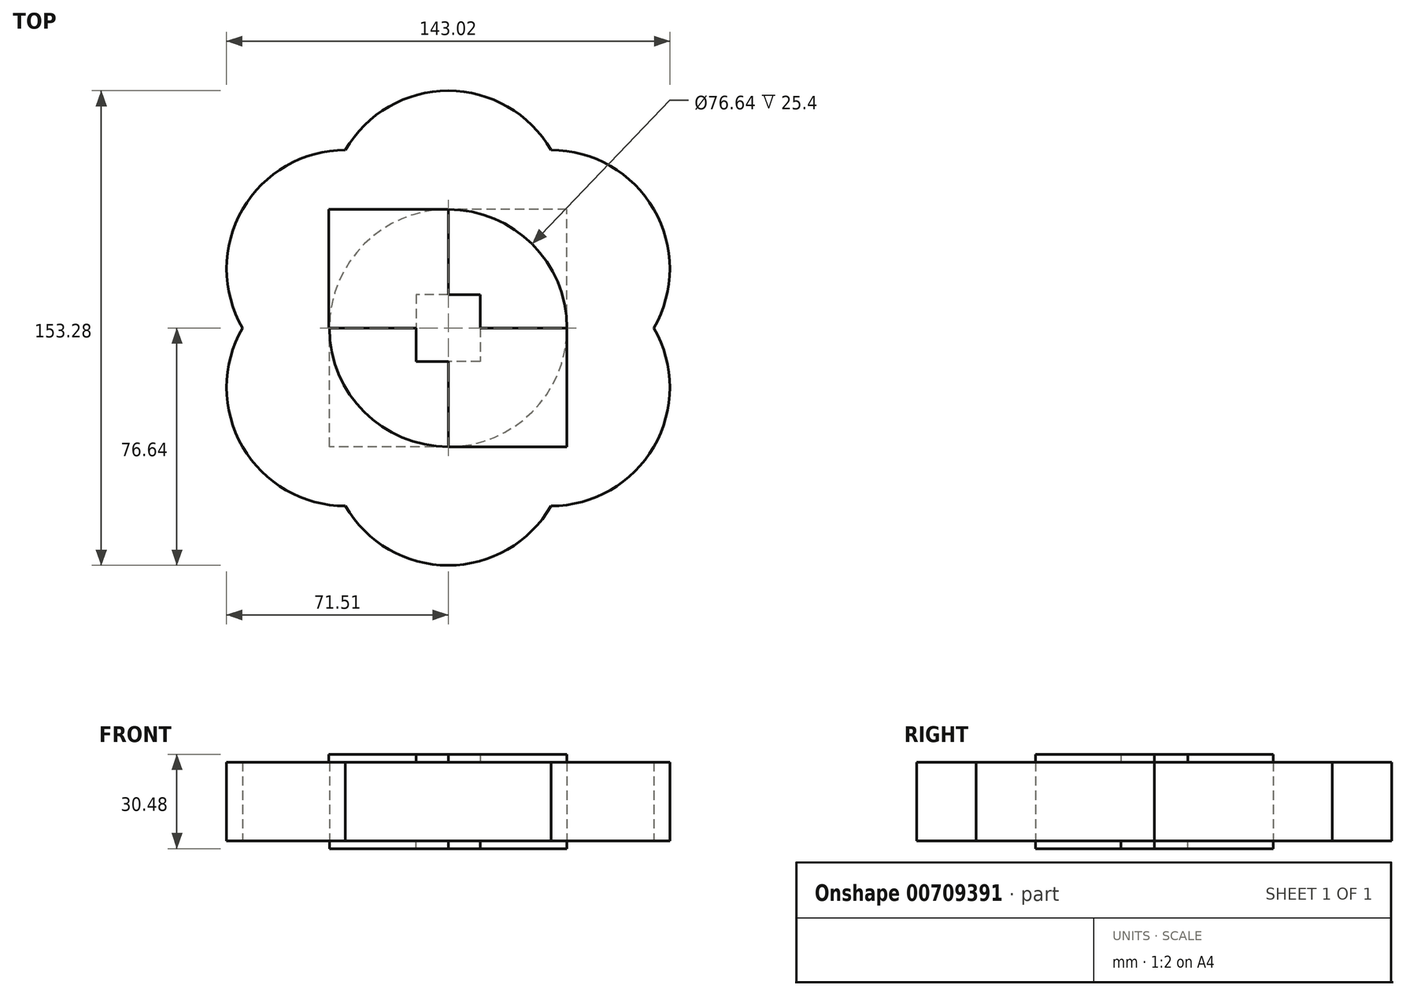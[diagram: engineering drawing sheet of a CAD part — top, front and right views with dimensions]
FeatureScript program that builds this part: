
annotation { "Feature Type Name" : "Feature", "Feature Type Description" : "" }
export const myFeature = defineFeature(function(context is Context, id is Id, definition is map)
    precondition{}
    {
        {
            var Q0;
            Q0=qCreatedBy(makeId("Top.planeOp"),FACE);
            var sketch = newSketch(context, id + "F0", { "sketchPlane" : qUnion([Q0])});
            skCircle(sketch, "E0", {"center": v(0, 0) * mm, "radius": 38.32 * mm});
            skCircle(sketch, "E1", {"center": v(0, 38.32) * mm, "radius": 38.32 * mm});
            skCircle(sketch, "E2", {"center": v(33.19, 19.16) * mm, "radius": 38.32 * mm});
            skCircle(sketch, "E3", {"center": v(33.19, -19.16) * mm, "radius": 38.32 * mm});
            skCircle(sketch, "E4", {"center": v(0, -38.32) * mm, "radius": 38.32 * mm});
            skCircle(sketch, "E5", {"center": v(-33.19, -19.16) * mm, "radius": 38.32 * mm});
            skCircle(sketch, "E6", {"center": v(-33.19, 19.16) * mm, "radius": 38.32 * mm});
            skSolve(sketch);
        }
        {
            var Q0;
            Q0 = qSketchRegion(id + "F0", true);
            extrude(context, id + "F1", {"entities" : qUnion([Q0]), "depth" : 25.4 * mm, "offsetDistance" : 25.4 * mm});
        }
        {
            var Q0;
            Q0=makeQuery(id+"F1.opExtrude","CAP_FACE",FACE,{"disambiguationData":[OSD([sQuery(id+"F0.wireOp",EDGE,"E0"),sQuery(id+"F0.wireOp",EDGE,"E1"),sQuery(id+"F0.wireOp",EDGE,"E2"),sQuery(id+"F0.wireOp",EDGE,"E3"),sQuery(id+"F0.wireOp",EDGE,"E4"),sQuery(id+"F0.wireOp",EDGE,"E5"),sQuery(id+"F0.wireOp",EDGE,"E6")])],"isStart":false});
            var sketch = newSketch(context, id + "F2", { "sketchPlane" : qUnion([Q0])});
            skPoint(sketch, "E7.center.orphan", {"position": v(38.32, 0) * mm});
            skPoint(sketch, "E8.center.orphan", {"position": v(0, -38.32) * mm});
            skPoint(sketch, "E9.center.orphan", {"position": v(0, 38.32) * mm});
            skPoint(sketch, "E10.center.orphan", {"position": v(-38.32, 0) * mm});
            skLineSegment(sketch, "E11.bottom", {"start": v(0, 0) * mm, "end": v(-38.51, 0) * mm});
            skLineSegment(sketch, "E11.top", {"start": v(0, 38.32) * mm, "end": v(-38.51, 38.32) * mm});
            skLineSegment(sketch, "E11.left", {"start": v(0, 0) * mm, "end": v(0, 38.32) * mm});
            skLineSegment(sketch, "E11.right", {"start": v(-38.51, 0) * mm, "end": v(-38.51, 38.32) * mm});
            skLineSegment(sketch, "E12.bottom", {"start": v(38.32, 0) * mm, "end": v(0, 0) * mm});
            skLineSegment(sketch, "E12.top", {"start": v(38.32, -38.32) * mm, "end": v(0, -38.32) * mm});
            skLineSegment(sketch, "E12.left", {"start": v(38.32, 0) * mm, "end": v(38.32, -38.32) * mm});
            skLineSegment(sketch, "E12.right", {"start": v(0, 0) * mm, "end": v(0, -38.32) * mm});
            skLineSegment(sketch, "E13.bottom", {"start": v(10.34, 10.79) * mm, "end": v(-10.34, 10.79) * mm});
            skLineSegment(sketch, "E13.top", {"start": v(10.34, -10.79) * mm, "end": v(-10.34, -10.79) * mm});
            skLineSegment(sketch, "E13.left", {"start": v(10.34, 10.79) * mm, "end": v(10.34, -10.79) * mm});
            skLineSegment(sketch, "E13.right", {"start": v(-10.34, 10.79) * mm, "end": v(-10.34, -10.79) * mm});
            skPoint(sketch, "E13.middle", {"position": v(0, 0) * mm});
            skSolve(sketch);
        }
        {
            var Q0;
            Q0 = qSketchRegion(id + "F2", true);
            extrude(context, id + "F3", {"entities" : qUnion([Q0]), "operationType" : NewBodyOperationType.ADD, "depth" : 2.54 * mm, "offsetDistance" : 25.4 * mm});
        }
        {
            var Q0;
            Q0=makeQuery(id+"F1.opExtrude","CAP_FACE",FACE,{"disambiguationData":[OSD([sQuery(id+"F0.wireOp",EDGE,"E0"),sQuery(id+"F0.wireOp",EDGE,"E1"),sQuery(id+"F0.wireOp",EDGE,"E2"),sQuery(id+"F0.wireOp",EDGE,"E3"),sQuery(id+"F0.wireOp",EDGE,"E4"),sQuery(id+"F0.wireOp",EDGE,"E5"),sQuery(id+"F0.wireOp",EDGE,"E6")])],"isStart":true});
            var sketch = newSketch(context, id + "F4", { "sketchPlane" : qUnion([Q0])});
            skPoint(sketch, "E14.bottom.start.orphan", {"position": v(-38.32, 0) * mm});
            skPoint(sketch, "E14.right.end.orphan", {"position": v(0, -38.32) * mm});
            skPoint(sketch, "E15.right.end.orphan", {"position": v(38.32, 0) * mm});
            skPoint(sketch, "E15.bottom.start.orphan", {"position": v(0, 38.32) * mm});
            skLineSegment(sketch, "E16.bottom", {"start": v(0, 38.32) * mm, "end": v(-38.32, 38.32) * mm});
            skLineSegment(sketch, "E16.top", {"start": v(0, 0) * mm, "end": v(-38.32, 0) * mm});
            skLineSegment(sketch, "E16.left", {"start": v(0, 38.32) * mm, "end": v(0, 0) * mm});
            skLineSegment(sketch, "E16.right", {"start": v(-38.32, 38.32) * mm, "end": v(-38.32, 0) * mm});
            skLineSegment(sketch, "E17.bottom", {"start": v(38.32, 0) * mm, "end": v(0, 0) * mm});
            skLineSegment(sketch, "E17.top", {"start": v(38.32, -38.32) * mm, "end": v(0, -38.32) * mm});
            skLineSegment(sketch, "E17.left", {"start": v(38.32, 0) * mm, "end": v(38.32, -38.32) * mm});
            skLineSegment(sketch, "E17.right", {"start": v(0, 0) * mm, "end": v(0, -38.32) * mm});
            skLineSegment(sketch, "E18.bottom", {"start": v(10.35, -10.79) * mm, "end": v(-10.35, -10.79) * mm});
            skLineSegment(sketch, "E18.top", {"start": v(10.35, 10.79) * mm, "end": v(-10.35, 10.79) * mm});
            skLineSegment(sketch, "E18.left", {"start": v(10.35, -10.79) * mm, "end": v(10.35, 10.79) * mm});
            skLineSegment(sketch, "E18.right", {"start": v(-10.35, -10.79) * mm, "end": v(-10.35, 10.79) * mm});
            skPoint(sketch, "E18.middle", {"position": v(0, 0) * mm});
            skSolve(sketch);
        }
        {
            var Q0;
            Q0 = qSketchRegion(id + "F4", true);
            extrude(context, id + "F5", {"entities" : qUnion([Q0]), "operationType" : NewBodyOperationType.ADD, "depth" : 2.54 * mm, "offsetDistance" : 25.4 * mm});
        }
    });
